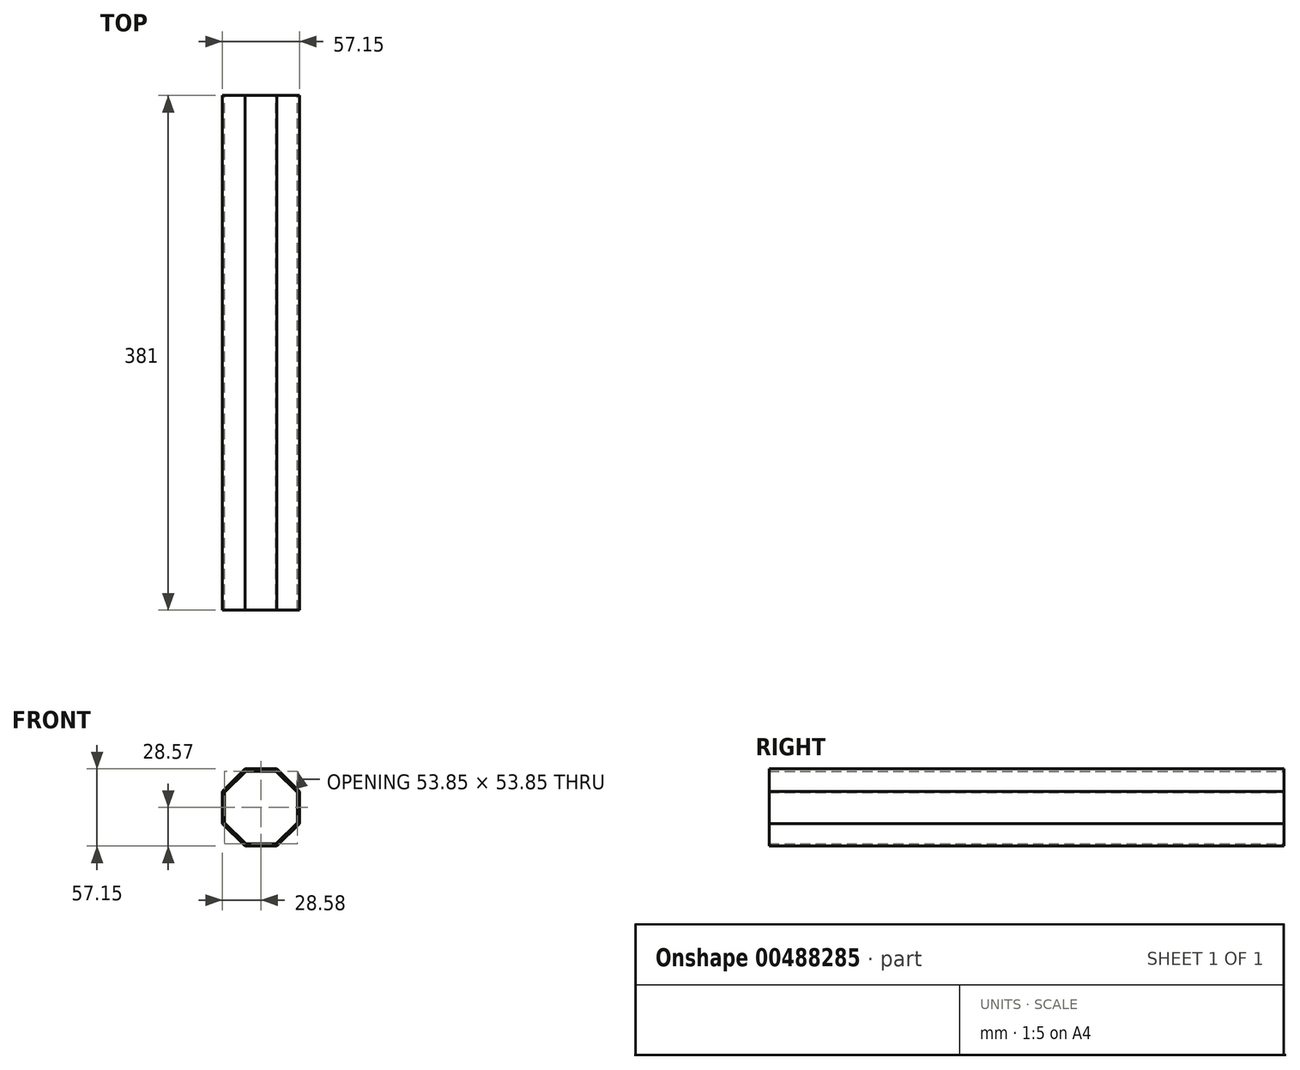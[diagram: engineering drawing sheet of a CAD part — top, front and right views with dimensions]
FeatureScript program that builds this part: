
annotation { "Feature Type Name" : "Feature", "Feature Type Description" : "" }
export const myFeature = defineFeature(function(context is Context, id is Id, definition is map)
    precondition{}
    {
        {
            var Q0;
            Q0=qCreatedBy(makeId("Front.planeOp"),FACE);
            var sketch = newSketch(context, id + "F0", { "sketchPlane" : qUnion([Q0])});
            skCircle(sketch, "E0.cCircle", {"center": v(0, 0) * mm, "radius": 28.58 * mm, "construction": true});
            skLineSegment(sketch, "E0.0", {"start": v(-11.84, 28.58) * mm, "end": v(11.84, 28.58) * mm});
            skLineSegment(sketch, "E0.1", {"start": v(11.84, 28.57) * mm, "end": v(28.57, 11.84) * mm});
            skLineSegment(sketch, "E0.2", {"start": v(28.58, 11.84) * mm, "end": v(28.58, -11.84) * mm});
            skLineSegment(sketch, "E0.3", {"start": v(28.57, -11.84) * mm, "end": v(11.84, -28.58) * mm});
            skLineSegment(sketch, "E0.4", {"start": v(11.84, -28.58) * mm, "end": v(-11.84, -28.58) * mm});
            skLineSegment(sketch, "E0.5", {"start": v(-11.84, -28.58) * mm, "end": v(-28.57, -11.84) * mm});
            skLineSegment(sketch, "E0.6", {"start": v(-28.57, -11.84) * mm, "end": v(-28.58, 11.84) * mm});
            skLineSegment(sketch, "E0.7", {"start": v(-28.58, 11.84) * mm, "end": v(-11.84, 28.58) * mm});
            skPoint(sketch, "E0.0.midPoint", {"position": v(0, 28.58) * mm});
            skCircle(sketch, "E1.cCircle", {"center": v(0, 0) * mm, "radius": 26.92 * mm, "construction": true});
            skLineSegment(sketch, "E1.0", {"start": v(-11.15, 26.92) * mm, "end": v(11.15, 26.92) * mm});
            skLineSegment(sketch, "E1.1", {"start": v(11.15, 26.92) * mm, "end": v(26.92, 11.15) * mm});
            skLineSegment(sketch, "E1.2", {"start": v(26.92, 11.15) * mm, "end": v(26.92, -11.15) * mm});
            skLineSegment(sketch, "E1.3", {"start": v(26.92, -11.15) * mm, "end": v(11.15, -26.92) * mm});
            skLineSegment(sketch, "E1.4", {"start": v(11.15, -26.92) * mm, "end": v(-11.15, -26.92) * mm});
            skLineSegment(sketch, "E1.5", {"start": v(-11.15, -26.92) * mm, "end": v(-26.92, -11.15) * mm});
            skLineSegment(sketch, "E1.6", {"start": v(-26.92, -11.15) * mm, "end": v(-26.92, 11.15) * mm});
            skLineSegment(sketch, "E1.7", {"start": v(-26.92, 11.15) * mm, "end": v(-11.15, 26.92) * mm});
            skPoint(sketch, "E1.0.midPoint", {"position": v(0, 26.92) * mm});
            skSolve(sketch);
        }
        {
            var Q0;
            Q0 = qSketchRegion(id + "F0", true);
            extrude(context, id + "F1", {"entities" : qUnion([Q0]), "depth" : 381 * mm});
        }
    });
